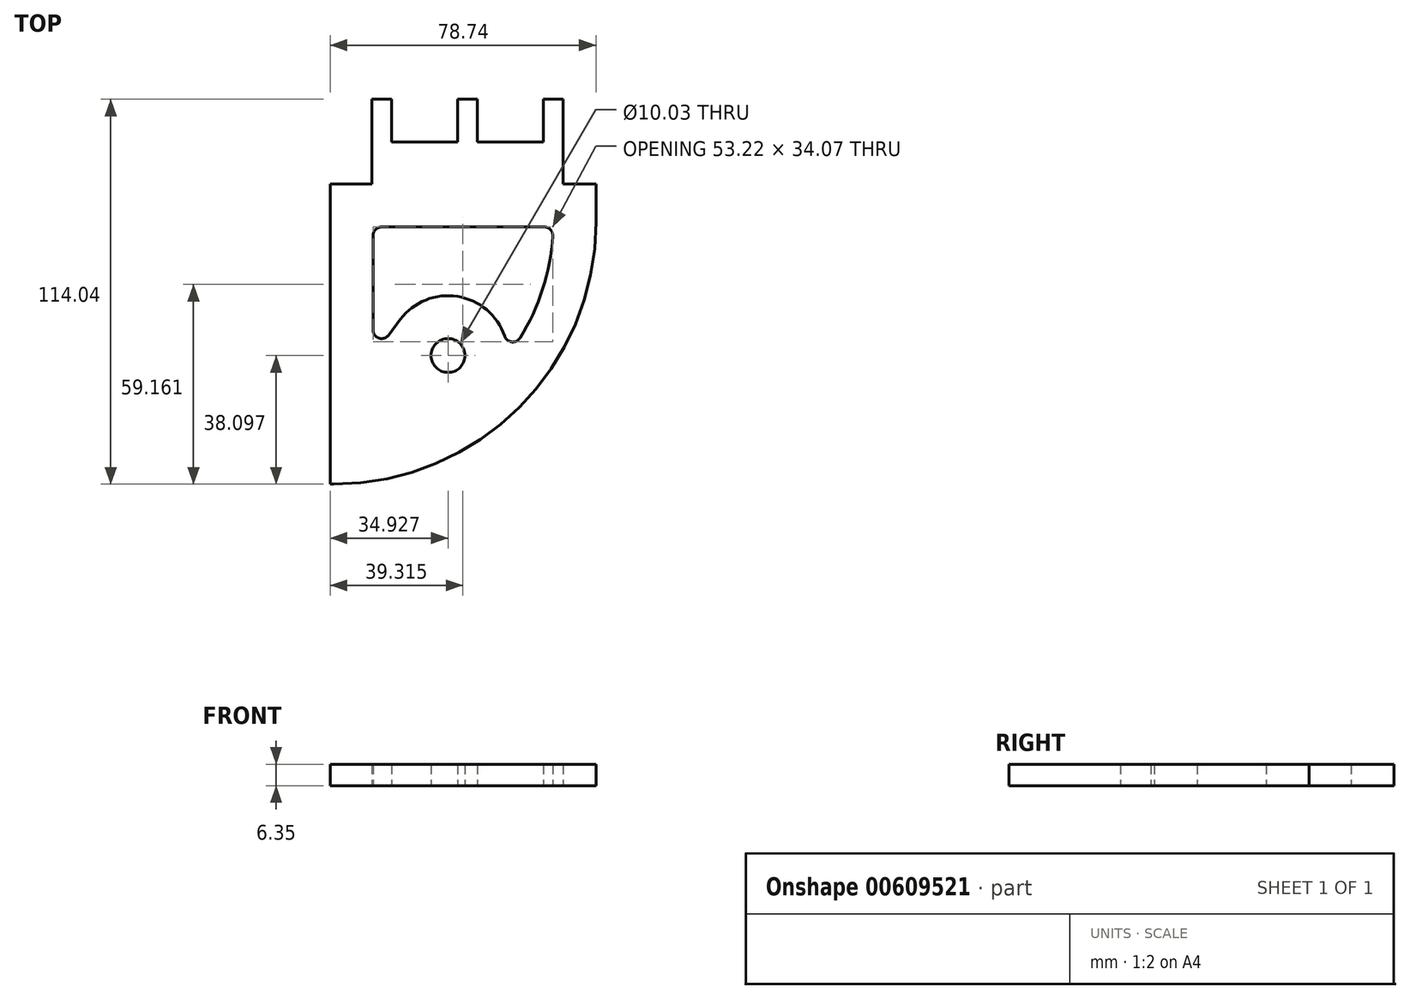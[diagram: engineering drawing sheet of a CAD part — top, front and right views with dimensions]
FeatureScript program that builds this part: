
annotation { "Feature Type Name" : "Feature", "Feature Type Description" : "" }
export const myFeature = defineFeature(function(context is Context, id is Id, definition is map)
    precondition{}
    {
        {
            var Q0;
            Q0=qCreatedBy(makeId("Top.planeOp"),FACE);
            var sketch = newSketch(context, id + "F0", { "sketchPlane" : qUnion([Q0])});
            skLineSegment(sketch, "E0.0", {"start": v(2.65, 34.25) * mm, "end": v(-16.9, 34.25) * mm});
            skLineSegment(sketch, "E0.1", {"start": v(33.9, 21.8) * mm, "end": v(33.9, 46.95) * mm});
            skLineSegment(sketch, "E0.2", {"start": v(-22.75, 21.8) * mm, "end": v(33.9, 21.8) * mm, "construction": true});
            skLineSegment(sketch, "E0.3", {"start": v(-22.75, 46.95) * mm, "end": v(-22.75, 21.8) * mm});
            skLineSegment(sketch, "E0.4", {"start": v(-16.9, 46.95) * mm, "end": v(-22.75, 46.95) * mm});
            skLineSegment(sketch, "E0.5", {"start": v(33.9, 46.95) * mm, "end": v(28.05, 46.95) * mm});
            skLineSegment(sketch, "E0.6", {"start": v(-16.9, 34.25) * mm, "end": v(-16.9, 46.95) * mm});
            skLineSegment(sketch, "E0.7", {"start": v(28.05, 46.95) * mm, "end": v(28.05, 34.25) * mm});
            skLineSegment(sketch, "E0.8", {"start": v(28.05, 34.25) * mm, "end": v(8.5, 34.25) * mm});
            skLineSegment(sketch, "E0.9", {"start": v(8.5, 34.25) * mm, "end": v(8.5, 46.95) * mm});
            skLineSegment(sketch, "E0.10", {"start": v(8.5, 46.95) * mm, "end": v(2.65, 46.95) * mm});
            skLineSegment(sketch, "E0.11", {"start": v(2.65, 46.95) * mm, "end": v(2.65, 34.25) * mm});
            skLineSegment(sketch, "E1", {"start": v(-22.75, 21.8) * mm, "end": v(-35.07, 21.8) * mm});
            skLineSegment(sketch, "E2", {"start": v(-35.07, 21.8) * mm, "end": v(-35.07, -67.1) * mm});
            skLineSegment(sketch, "E3", {"start": v(33.9, 21.8) * mm, "end": v(43.67, 21.8) * mm});
            skLineSegment(sketch, "E4", {"start": v(43.67, 21.8) * mm, "end": v(43.67, 10.53) * mm});
            skLineSegment(sketch, "E5", {"start": v(-35.07, -67.1) * mm, "end": v(-33.95, -67.1) * mm});
            skCircle(sketch, "E6", {"center": v(-0.14, -29) * mm, "radius": 31.75 * mm, "construction": true});
            skCircle(sketch, "E7", {"center": v(-0.14, -29) * mm, "radius": 5.02 * mm});
            skLineSegment(sketch, "E8", {"start": v(-35.07, -46.58) * mm, "end": v(-29.58, -46.58) * mm, "construction": true});
            skLineSegment(sketch, "E9", {"start": v(-33.95, -67.1) * mm, "end": v(-33.95, -34.7) * mm, "construction": true});
            skArc(sketch, "E10", {"start": v(-29.58, -46.58) * mm, "mid": v(32.03, -17.14) * mm, "end": v(-33.95, -34.7) * mm, "construction": true});
            skCircle(sketch, "E11", {"center": v(-28.08, -62.33) * mm, "radius": 3.18 * mm, "construction": true});
            skPoint(sketch, "E12.visualSharp", {"position": v(43.67, -67.1) * mm});
            skArc(sketch, "E12.filletArc", {"start": v(-33.95, -67.1) * mm, "mid": v(20.94, -44.36) * mm, "end": v(43.67, 10.53) * mm});
            skLineSegment(sketch, "E13", {"start": v(30.97, 9.1) * mm, "end": v(-22.37, 9.1) * mm});
            skLineSegment(sketch, "E14", {"start": v(-22.37, 9.1) * mm, "end": v(-22.37, -29) * mm});
            skArc(sketch, "E15", {"start": v(17.57, -29) * mm, "mid": v(27.31, -11.01) * mm, "end": v(30.97, 9.1) * mm});
            skArc(sketch, "E16", {"start": v(17.57, -29) * mm, "mid": v(5.5, -12.2) * mm, "end": v(-14.27, -18.3) * mm});
            skLineSegment(sketch, "E17", {"start": v(-14.27, -18.3) * mm, "end": v(-22.37, -29) * mm});
            skLineSegment(sketch, "E18", {"start": v(-0.14, -29) * mm, "end": v(-22.37, -29) * mm, "construction": true});
            skSolve(sketch);
        }
        {
            var Q0;
            Q0 = qSketchRegion(id + "F0", true);
            extrude(context, id + "F1", {"entities" : qUnion([Q0]), "depth" : 6.35 * mm, "offsetDistance" : 25.4 * mm});
        }
        {
            var Q0;
            Q0=makeQuery(id+"F1.opExtrude","SWEPT_EDGE",EDGE,{"disambiguationData":[OSD([sQuery(id+"F0.wireOp",EDGE,"E13"),sQuery(id+"F0.wireOp",EDGE,"E15")])]});
            var Q1;
            Q1=makeQuery(id+"F1.opExtrude","SWEPT_EDGE",EDGE,{"disambiguationData":[OSD([sQuery(id+"F0.wireOp",EDGE,"E13"),sQuery(id+"F0.wireOp",EDGE,"E14")])]});
            var Q2;
            Q2=makeQuery(id+"F1.opExtrude","SWEPT_EDGE",EDGE,{"disambiguationData":[OSD([sQuery(id+"F0.wireOp",EDGE,"E15"),sQuery(id+"F0.wireOp",EDGE,"E16")])]});
            var Q3;
            Q3=makeQuery(id+"F1.opExtrude","SWEPT_EDGE",EDGE,{"disambiguationData":[OSD([sQuery(id+"F0.wireOp",EDGE,"E14"),sQuery(id+"F0.wireOp",EDGE,"E17")])]});
            fillet(context, id + "F2", {"entities" : qUnion([Q0, Q1, Q2, Q3]), "radius" : 2.54 * mm, "tangentPropagation" : true, "allowEdgeOverflow" : false});
        }
    });
